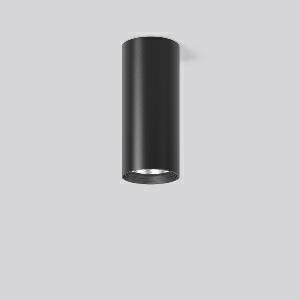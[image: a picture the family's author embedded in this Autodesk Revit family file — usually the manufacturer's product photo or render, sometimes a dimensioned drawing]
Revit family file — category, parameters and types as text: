
# Revit family: heledon_mini_a_931209_003_d85f
name_source: partatom
category: Lighting Fixtures
units: mm (PartAtom-declared; Revit-internal decimal feet)

## family parameters
Cut with Voids When Loaded = No
Host = Face
Light Source = No
Part Type = Normal
Room Calculation Point = No
Round Connector Dimension = Use Diameter
Shared = No

## types (1)
- HELEDON mini A (1 x LED Modul 930, 3500 lm, 3000)
    Apparent Load = 29 VA
    Approval mark = CE
    CIE Flux Codes = 99 100 100 100 100
    Color Rendering = 90
    Color Temperature = 3000
    Default Elevation = 1800 mm
    Description = Series: HELEDON mini
Cylindrical surface-mounted downlight. Housing: die-cast aluminium, powder-coated. Internal ceiling frame polycarbonate with bayonet mounting. Black plastic ring and recessed LED to prevent glare from the side. Optical assembly with reflector made of MIRO-Silver with 98% total light reflection for outstanding efficiency - can be changed without tools. Best colour rendering index Ra>90. Suitable for Ceiling mounting. Easy installation with a separate ceiling frame with bayonet mounting and plug connection. Driver integrated. Connected via plug-in connector. High quality converter without flickering and stroboscopic effect. The following accessories can be mounted without use of tools: interchangeable lenses, decorative glasses, honeycomb louvre, clear and frosted diffusers, white interchangeable plastic ring. 
Colour: deep black, matt (RAL 9005)
Diameter: 87 mm
Height: 197 mm
Lamp: LED
Socket: without socket
Colour temperature: 3000K
Colour rendering index (CRI): 92
System power: 29 W
Rated luminous flux: 3500 lm
Luminous efficiency: 121 lm/W
Control gear: Regulated power supply
Protection class: I
Type of protection: IP 20
    Height = 197 mm
    Lamp = 1 x LED Modul 930
    Lamp Light Flux = 3500 lm
    Lamp count = 1
    Length = 87 mm
    Lifetime = 50000 h
    Luminous efficacy = 121 lm/W
    Manufacturer = RZB
    ModVariant = No
    Model = 931209.003
    Mounting Place = Ceiling
    Mounting Type = Surface mounted
    Number of Poles = 1
    OnlyDefault = Yes
    Power Factor = 1
    Product Name = HELEDON mini A
    Product group = Surface mounted downlights
    ProductGroupID = 302
    Protection Class = Protection class I
    Protection Degree = IP 20
    RLX_Detail_Level = 1
    RLX_Emergency_Light_Flux = 0 lm
    RLX_Emergency_Type = 0
    RLX_Emergency_Type_DB = No
    RlxData = <blob elided: 107061 chars, md5=075cbd38>
    Socket = socket
    Standby Power = 0 W
    System Light Flux = 3500 lm
    System Power = 29 W
    Type Comments = Product without accessories
    Type Image = 931188.003.jpg
    URL = http://relux.com
    VarID = ---
    Voltage = 230 V
    Voltage Range = 220-240 V
    Weight = 0.00 kg
    Width = 0 mm  [stored 0 ft]

note: [stored X ft] marks values corroborated as IEEE doubles in the binary element streams (Revit-internal decimal feet)

## geometry (parser evidence)
native form markers: Blend x4, Sweep x9
no freeform markers — native parametric forms only
